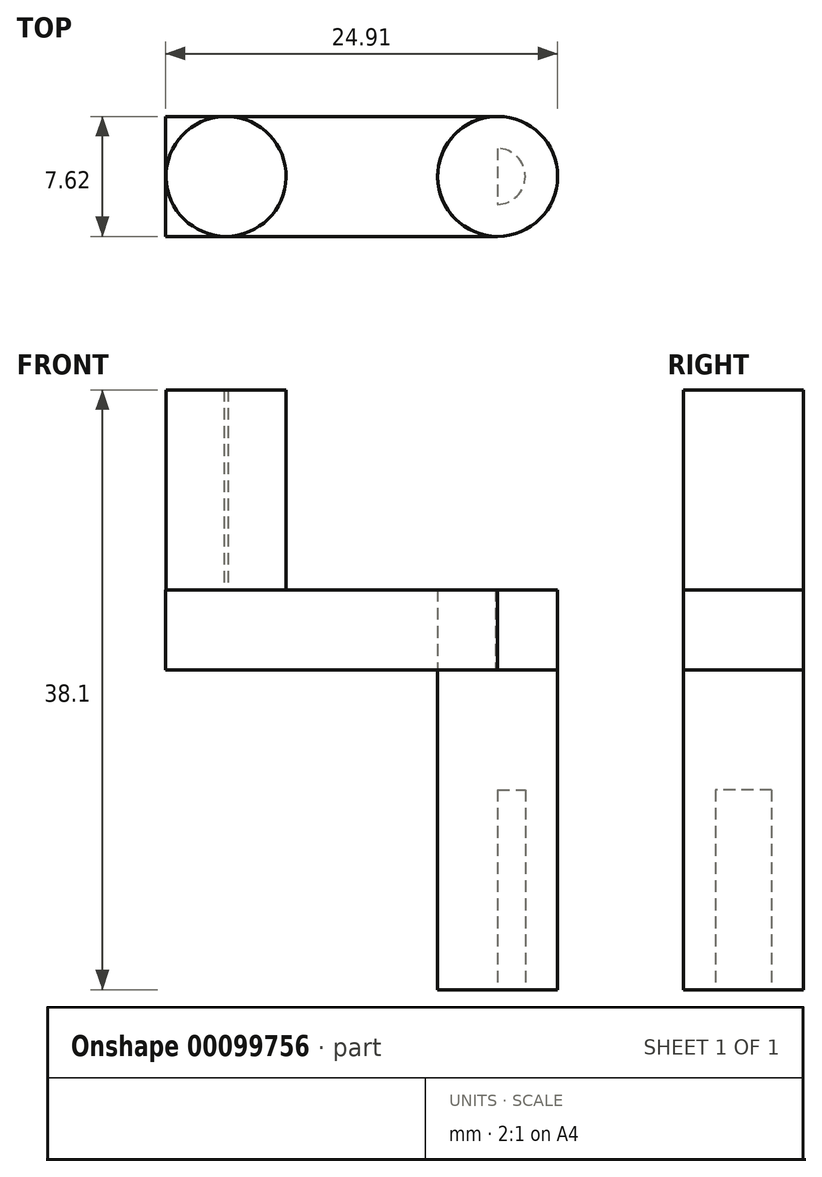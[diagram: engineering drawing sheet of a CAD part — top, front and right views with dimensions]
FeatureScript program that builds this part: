
annotation { "Feature Type Name" : "Feature", "Feature Type Description" : "" }
export const myFeature = defineFeature(function(context is Context, id is Id, definition is map)
    precondition{}
    {
        {
            var Q0;
            Q0=qCreatedBy(makeId("Top.planeOp"),FACE);
            var sketch = newSketch(context, id + "F0", { "sketchPlane" : qUnion([Q0])});
            skCircle(sketch, "E0", {"center": v(0, 0) * mm, "radius": 3.8 * mm});
            skSolve(sketch);
        }
        {
            var Q0;
            Q0=makeQuery(id+"F0.imprint","IMPRINT",FACE,{"disambiguationData":[TD([[makeQuery(id+"F0.imprint","IMPRINT",EDGE,{"derivedFrom":sQuery(id+"F0.wireOp",EDGE,"E0")}),1.0]])]});
            extrude(context, id + "F1", {"entities" : qUnion([Q0]), "depth" : 20.32 * mm});
        }
        {
            var Q0;
            Q0=makeQuery(id+"F1.opExtrude","CAP_FACE",FACE,{"disambiguationData":[OSD([sQuery(id+"F0.wireOp",EDGE,"E0")])],"isStart":true});
            var sketch = newSketch(context, id + "F2", { "sketchPlane" : qUnion([Q0])});
            skCircle(sketch, "E1", {"center": v(0, 0) * mm, "radius": 1.78 * mm});
            skArc(sketch, "E2", {"start": v(0, -1.78) * mm, "mid": v(1.75, 0) * mm, "end": v(0, 1.78) * mm});
            skLineSegment(sketch, "E3", {"start": v(0, -1.78) * mm, "end": v(0, 1.78) * mm});
            skSolve(sketch);
        }
        {
            var Q0;
            Q0=makeQuery(id+"F2.imprint","IMPRINT",FACE,{"disambiguationData":[TD([[makeQuery(id+"F2.imprint","IMPRINT",EDGE,{"derivedFrom":sQuery(id+"F2.wireOp",EDGE,"E2")}),1.0]])]});
            extrude(context, id + "F3", {"entities" : qUnion([Q0]), "operationType" : NewBodyOperationType.REMOVE, "oppositeDirection" : true, "depth" : 12.7 * mm});
        }
        {
            var Q0;
            Q0=makeQuery(id+"F1.opExtrude","CAP_FACE",FACE,{"disambiguationData":[OSD([sQuery(id+"F0.wireOp",EDGE,"E0")])],"isStart":false});
            var sketch = newSketch(context, id + "F4", { "sketchPlane" : qUnion([Q0])});
            skLineSegment(sketch, "E4.bottom", {"start": v(0, -3.8) * mm, "end": v(-21.1, -3.8) * mm});
            skLineSegment(sketch, "E4.top", {"start": v(0, 3.8) * mm, "end": v(-21.1, 3.8) * mm});
            skLineSegment(sketch, "E4.left", {"start": v(0, -3.8) * mm, "end": v(0, 3.8) * mm});
            skLineSegment(sketch, "E4.right", {"start": v(-21.1, -3.8) * mm, "end": v(-21.1, 3.8) * mm});
            skSolve(sketch);
        }
        {
            var Q0;
            {var subQ0=sQuery(id+"F4.wireOp",EDGE,"E4.bottom");Q0=makeQuery(id+"F4.imprint","IMPRINT",FACE,{"disambiguationData":[TD([[makeQuery(id+"F4.imprint","IMPRINT",EDGE,{"derivedFrom":subQ0}),-1.0]])]});}
            extrude(context, id + "F5", {"entities" : qUnion([Q0]), "depth" : 5.08 * mm});
        }
        {
            var Q0;
            Q0=makeQuery(id+"F1.opExtrude","CAP_FACE",FACE,{"disambiguationData":[OSD([sQuery(id+"F0.wireOp",EDGE,"E0")])],"isStart":false});
            var sketch = newSketch(context, id + "F6", { "sketchPlane" : qUnion([Q0])});
            skCircle(sketch, "E5", {"center": v(0, 0) * mm, "radius": 3.81 * mm});
            skSolve(sketch);
        }
        {
            var Q0;
            Q0=makeQuery(id+"F6.imprint","IMPRINT",FACE,{"disambiguationData":[TD([[makeQuery(id+"F6.imprint","IMPRINT",EDGE,{"derivedFrom":sQuery(id+"F6.wireOp",EDGE,"E5")}),1.0]])]});
            extrude(context, id + "F7", {"entities" : qUnion([Q0]), "depth" : 5.08 * mm});
        }
        {
            var Q0;
            Q0=makeQuery(id+"F5.opExtrude","CAP_FACE",FACE,{"disambiguationData":[OSD([sQuery(id+"F0.wireOp",EDGE,"E0"),sQuery(id+"F4.wireOp",EDGE,"E4.bottom"),sQuery(id+"F4.wireOp",EDGE,"E4.top"),sQuery(id+"F4.wireOp",EDGE,"E4.right")])],"isStart":false});
            var sketch = newSketch(context, id + "F8", { "sketchPlane" : qUnion([Q0])});
            skCircle(sketch, "E6", {"center": v(-17.25, 0) * mm, "radius": 3.81 * mm});
            skSolve(sketch);
        }
        {
            var Q0;
            {var subQ0=sQuery(id+"F8.wireOp",EDGE,"E6");var subQ1=makeQuery(id+"F5.opExtrude","CAP_EDGE",EDGE,{"disambiguationData":[OSD([sQuery(id+"F4.wireOp",EDGE,"E4.top")])],"isStart":false});var subQ2=makeQuery(id+"F8.imprint","INTERSECT",VERTEX,{"disambiguationData":[OD(0.0)],"derivedFrom":[subQ1,subQ0]});Q0=makeQuery(id+"F8.imprint","IMPRINT",FACE,{"disambiguationData":[TD([[makeQuery(id+"F8.imprint","IMPRINT",EDGE,{"disambiguationData":[TD([[subQ2,-1.0]])],"derivedFrom":subQ0}),1.0]])]});}
            extrude(context, id + "F9", {"entities" : qUnion([Q0]), "operationType" : NewBodyOperationType.ADD, "depth" : 12.7 * mm});
        }
    });
